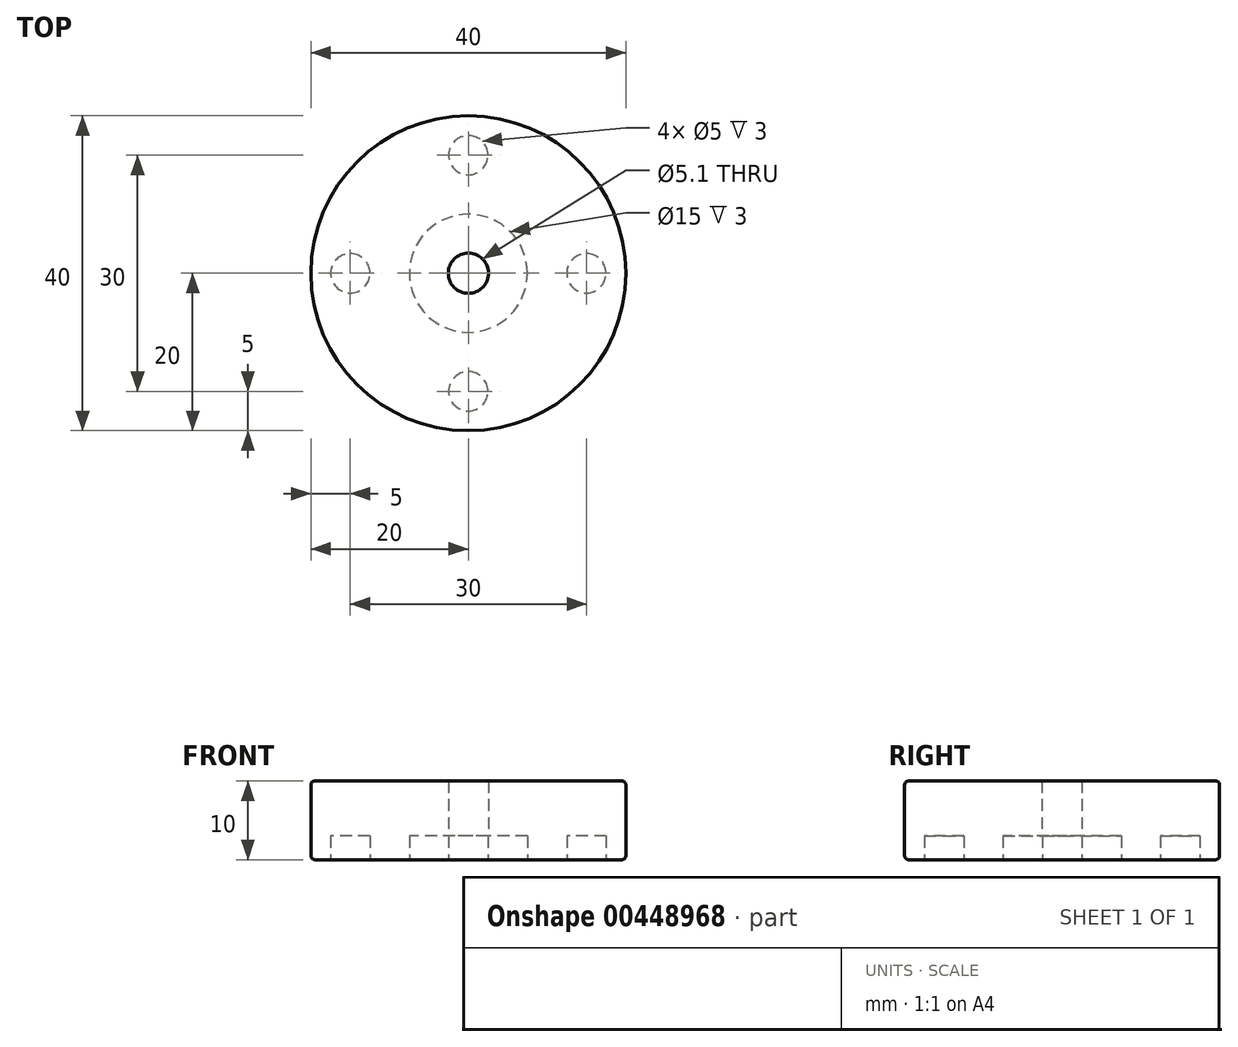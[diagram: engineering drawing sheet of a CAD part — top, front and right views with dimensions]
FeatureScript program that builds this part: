
annotation { "Feature Type Name" : "Feature", "Feature Type Description" : "" }
export const myFeature = defineFeature(function(context is Context, id is Id, definition is map)
    precondition{}
    {
        {
            var Q0;
            Q0=qCreatedBy(makeId("Top.planeOp"),FACE);
            var sketch = newSketch(context, id + "F0", { "sketchPlane" : qUnion([Q0])});
            skCircle(sketch, "E0", {"center": v(0, 0) * mm, "radius": 20 * mm});
            skCircle(sketch, "E1", {"center": v(0, 0) * mm, "radius": 7.5 * mm});
            skCircle(sketch, "E2", {"center": v(0, 15) * mm, "radius": 2.5 * mm});
            skCircle(sketch, "E3.1.0", {"center": v(-15, 0) * mm, "radius": 2.5 * mm});
            skCircle(sketch, "E3.2.0", {"center": v(0, -15) * mm, "radius": 2.5 * mm});
            skCircle(sketch, "E4.1.3.0", {"center": v(15, 0) * mm, "radius": 2.5 * mm});
            skCircle(sketch, "E5", {"center": v(0, 0) * mm, "radius": 2.55 * mm});
            skSolve(sketch);
        }
        {
            var Q0;
            Q0=makeQuery(id+"F0.imprint","IMPRINT",FACE,{"disambiguationData":[TD([[makeQuery(id+"F0.imprint","IMPRINT",EDGE,{"derivedFrom":sQuery(id+"F0.wireOp",EDGE,"E0")}),1.0]])]});
            var Q1;
            Q1=makeQuery(id+"F0.imprint","IMPRINT",FACE,{"disambiguationData":[TD([[makeQuery(id+"F0.imprint","IMPRINT",EDGE,{"derivedFrom":sQuery(id+"F0.wireOp",EDGE,"E3.1.0")}),1.0]])]});
            var Q2;
            Q2=makeQuery(id+"F0.imprint","IMPRINT",FACE,{"disambiguationData":[TD([[makeQuery(id+"F0.imprint","IMPRINT",EDGE,{"derivedFrom":sQuery(id+"F0.wireOp",EDGE,"E1")}),1.0]])]});
            var Q3;
            Q3=makeQuery(id+"F0.imprint","IMPRINT",FACE,{"disambiguationData":[TD([[makeQuery(id+"F0.imprint","IMPRINT",EDGE,{"derivedFrom":sQuery(id+"F0.wireOp",EDGE,"E4.1.3.0")}),1.0]])]});
            var Q4;
            Q4=makeQuery(id+"F0.imprint","IMPRINT",FACE,{"disambiguationData":[TD([[makeQuery(id+"F0.imprint","IMPRINT",EDGE,{"derivedFrom":sQuery(id+"F0.wireOp",EDGE,"E3.2.0")}),1.0]])]});
            var Q5;
            Q5=makeQuery(id+"F0.imprint","IMPRINT",FACE,{"disambiguationData":[TD([[makeQuery(id+"F0.imprint","IMPRINT",EDGE,{"derivedFrom":sQuery(id+"F0.wireOp",EDGE,"E2")}),1.0]])]});
            extrude(context, id + "F1", {"entities" : qUnion([Q0, Q1, Q2, Q3, Q4, Q5]), "depth" : 10 * mm});
        }
        {
            var Q0;
            Q0=makeQuery(id+"F0.imprint","IMPRINT",FACE,{"disambiguationData":[TD([[makeQuery(id+"F0.imprint","IMPRINT",EDGE,{"derivedFrom":sQuery(id+"F0.wireOp",EDGE,"E2")}),1.0]])]});
            var Q1;
            Q1=makeQuery(id+"F0.imprint","IMPRINT",FACE,{"disambiguationData":[TD([[makeQuery(id+"F0.imprint","IMPRINT",EDGE,{"derivedFrom":sQuery(id+"F0.wireOp",EDGE,"E3.1.0")}),1.0]])]});
            var Q2;
            Q2=makeQuery(id+"F0.imprint","IMPRINT",FACE,{"disambiguationData":[TD([[makeQuery(id+"F0.imprint","IMPRINT",EDGE,{"derivedFrom":sQuery(id+"F0.wireOp",EDGE,"E3.2.0")}),1.0]])]});
            var Q3;
            Q3=makeQuery(id+"F0.imprint","IMPRINT",FACE,{"disambiguationData":[TD([[makeQuery(id+"F0.imprint","IMPRINT",EDGE,{"derivedFrom":sQuery(id+"F0.wireOp",EDGE,"E4.1.3.0")}),1.0]])]});
            var Q4;
            Q4=makeQuery(id+"F0.imprint","IMPRINT",FACE,{"disambiguationData":[TD([[makeQuery(id+"F0.imprint","IMPRINT",EDGE,{"derivedFrom":sQuery(id+"F0.wireOp",EDGE,"E1")}),1.0]])]});
            extrude(context, id + "F2", {"entities" : qUnion([Q0, Q1, Q2, Q3, Q4]), "operationType" : NewBodyOperationType.REMOVE, "depth" : 3 * mm});
        }
        {
            var Q0;
            Q0=makeQuery(id+"F2.boolean.opBoolean","COPY",EDGE,{"derivedFrom":makeQuery(id+"F2.opExtrude","CAP_EDGE",EDGE,{"disambiguationData":[OSD([sQuery(id+"F0.wireOp",EDGE,"E5")])],"isStart":false})});
            var Q1;
            Q1=makeQuery(id+"F1.opExtrude","CAP_EDGE",EDGE,{"disambiguationData":[OSD([sQuery(id+"F0.wireOp",EDGE,"E0")])],"isStart":true});
            var Q2;
            Q2=makeQuery(id+"F1.opExtrude","CAP_EDGE",EDGE,{"disambiguationData":[OSD([sQuery(id+"F0.wireOp",EDGE,"E0")])],"isStart":false});
            fillet(context, id + "F3", {"entities" : qUnion([Q0, Q1, Q2]), "radius" : 0.5 * mm, "tangentPropagation" : true, "allowEdgeOverflow" : false});
        }
    });
